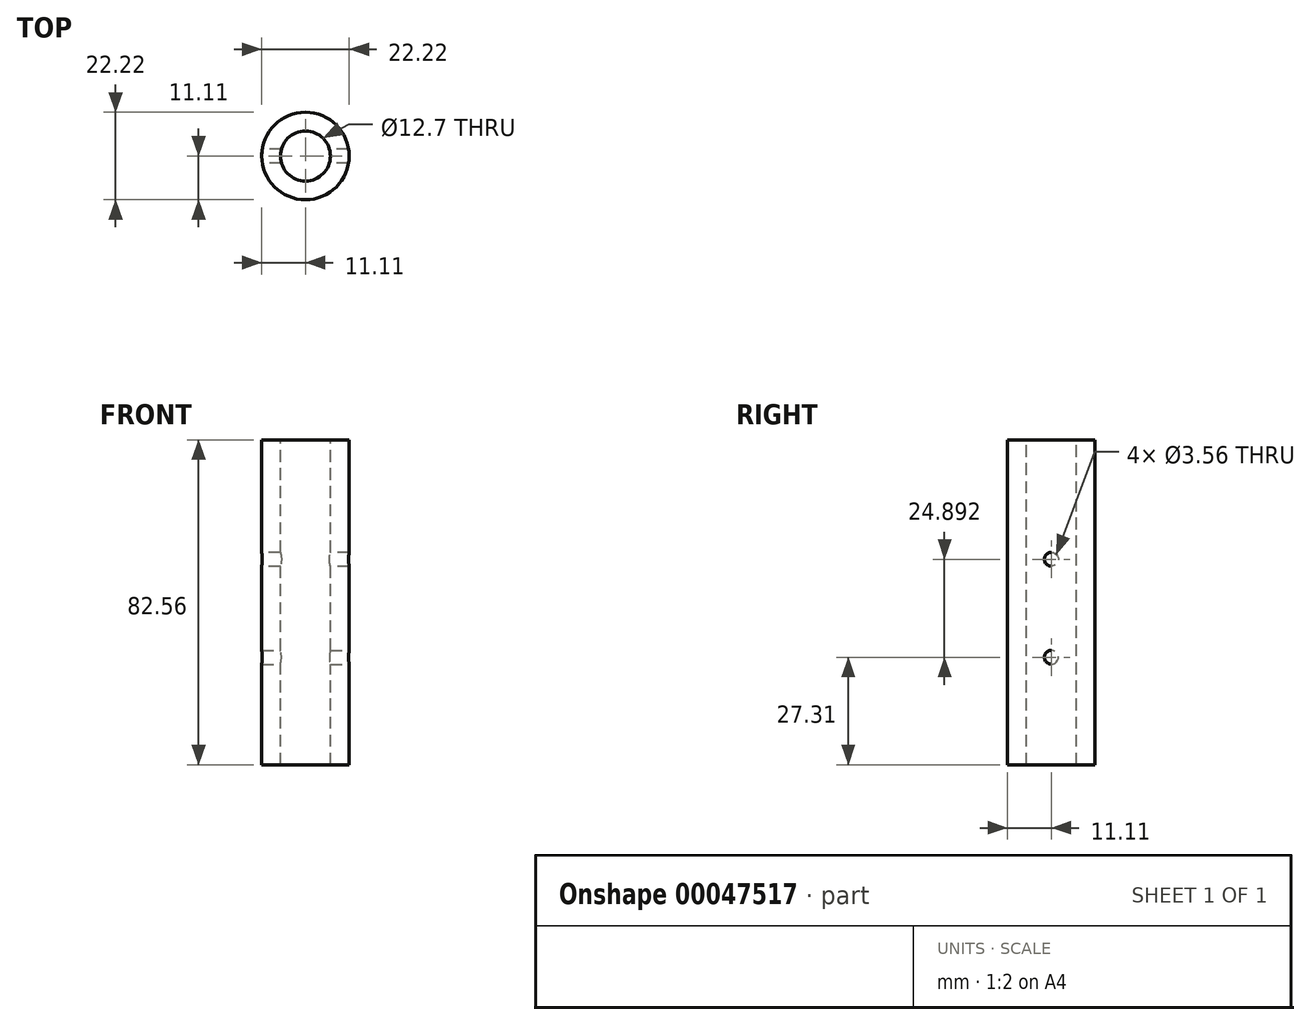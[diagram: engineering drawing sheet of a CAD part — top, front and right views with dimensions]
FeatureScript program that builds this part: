
annotation { "Feature Type Name" : "Feature", "Feature Type Description" : "" }
export const myFeature = defineFeature(function(context is Context, id is Id, definition is map)
    precondition{}
    {
        {
            var Q0;
            Q0=qCreatedBy(makeId("Top.planeOp"),FACE);
            var sketch = newSketch(context, id + "F0", { "sketchPlane" : qUnion([Q0])});
            skCircle(sketch, "E0", {"center": v(0, 0) * mm, "radius": 11.11 * mm});
            skSolve(sketch);
        }
        {
            var Q0;
            Q0=makeQuery(id+"F0.imprint","IMPRINT",FACE,{"disambiguationData":[TD([[makeQuery(id+"F0.imprint","IMPRINT",EDGE,{"derivedFrom":sQuery(id+"F0.wireOp",EDGE,"E0")}),1.0]])]});
            extrude(context, id + "F1", {"entities" : qUnion([Q0]), "endBound" : BoundingType.SYMMETRIC, "depth" : 82.55 * mm});
        }
        {
            var Q0;
            Q0=makeQuery(id+"F1.opExtrude","CAP_FACE",FACE,{"disambiguationData":[OSD([sQuery(id+"F0.wireOp",EDGE,"E0")])],"isStart":false});
            var sketch = newSketch(context, id + "F2", { "sketchPlane" : qUnion([Q0])});
            skCircle(sketch, "E1", {"center": v(0, 0) * mm, "radius": 6.35 * mm});
            skSolve(sketch);
        }
        {
            var Q0;
            Q0=makeQuery(id+"F2.imprint","IMPRINT",FACE,{"disambiguationData":[TD([[makeQuery(id+"F2.imprint","IMPRINT",EDGE,{"derivedFrom":sQuery(id+"F2.wireOp",EDGE,"E1")}),1.0]])]});
            var Q1;
            Q1=makeQuery(id+"F1.opExtrude","CAP_FACE",FACE,{"disambiguationData":[OSD([sQuery(id+"F0.wireOp",EDGE,"E0")])],"isStart":true});
            extrude(context, id + "F3", {"entities" : qUnion([Q0]), "operationType" : NewBodyOperationType.REMOVE, "endBound" : BoundingType.UP_TO_SURFACE, "oppositeDirection" : true, "endBoundEntityFace" : qUnion([Q1]), "depth" : 25.4 * mm});
        }
        {
            var Q0;
            Q0=qCreatedBy(makeId("Right.planeOp"),FACE);
            var sketch = newSketch(context, id + "F4", { "sketchPlane" : qUnion([Q0])});
            skCircle(sketch, "E2", {"center": v(0, 10.92) * mm, "radius": 1.78 * mm});
            skSolve(sketch);
        }
        {
            var Q0;
            Q0 = qSketchRegion(id + "F4", true);
            var Q1;
            Q1=makeQuery(id+"F1.opExtrude","SWEPT_FACE",FACE,{"disambiguationData":[OSD([sQuery(id+"F0.wireOp",EDGE,"E0")])]});
            extrude(context, id + "F5", {"entities" : qUnion([Q0]), "operationType" : NewBodyOperationType.REMOVE, "endBound" : BoundingType.SYMMETRIC, "endBoundEntityFace" : qUnion([Q1]), "depth" : 22.22 * mm});
        }
        {
            var Q0;
            Q0=qCreatedBy(makeId("Right.planeOp"),FACE);
            var sketch = newSketch(context, id + "F6", { "sketchPlane" : qUnion([Q0])});
            skCircle(sketch, "E3", {"center": v(0, -13.97) * mm, "radius": 1.78 * mm});
            skSolve(sketch);
        }
        {
            var Q0;
            Q0 = qSketchRegion(id + "F6", true);
            extrude(context, id + "F7", {"entities" : qUnion([Q0]), "operationType" : NewBodyOperationType.REMOVE, "endBound" : BoundingType.SYMMETRIC, "oppositeDirection" : true, "depth" : 22.22 * mm});
        }
    });
